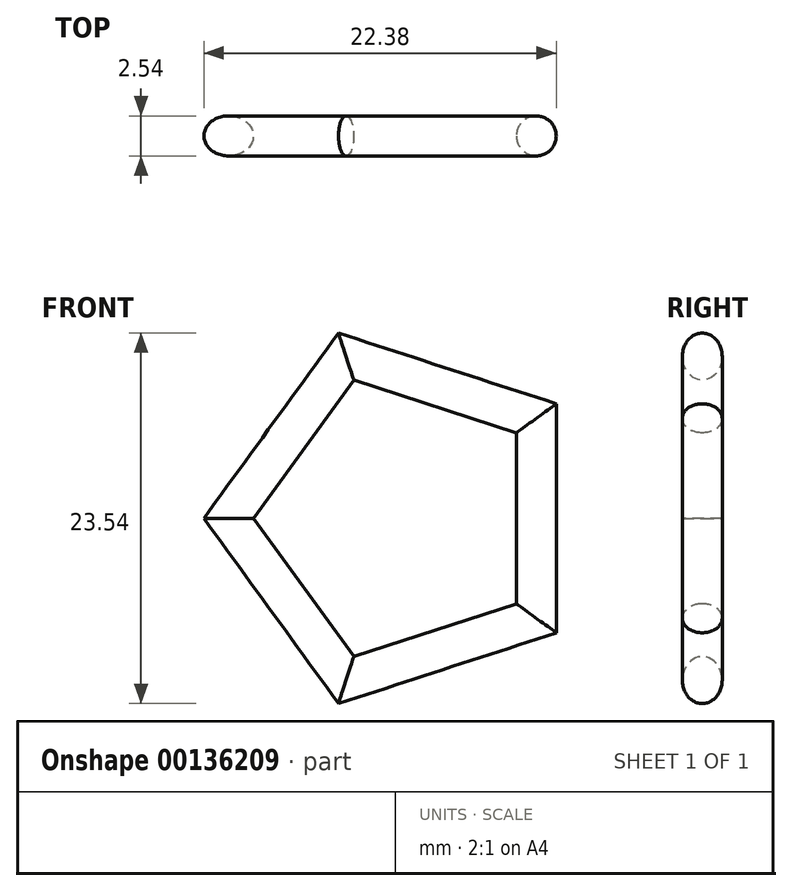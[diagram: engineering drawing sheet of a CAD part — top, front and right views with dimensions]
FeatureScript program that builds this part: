
annotation { "Feature Type Name" : "Feature", "Feature Type Description" : "" }
export const myFeature = defineFeature(function(context is Context, id is Id, definition is map)
    precondition{}
    {
        {
            var Q0;
            Q0=qCreatedBy(makeId("Front.planeOp"),FACE);
            var sketch = newSketch(context, id + "F0", { "sketchPlane" : qUnion([Q0])});
            skCircle(sketch, "E0.cCircle", {"center": v(0, 0) * mm, "radius": 11 * mm, "construction": true});
            skLineSegment(sketch, "E0.0", {"start": v(11, 6.35) * mm, "end": v(11, -6.35) * mm});
            skLineSegment(sketch, "E0.1", {"start": v(11, -6.35) * mm, "end": v(0, -12.7) * mm});
            skLineSegment(sketch, "E0.2", {"start": v(0, -12.7) * mm, "end": v(-11, -6.35) * mm});
            skLineSegment(sketch, "E0.3", {"start": v(-11, -6.35) * mm, "end": v(-11, 6.35) * mm});
            skLineSegment(sketch, "E0.4", {"start": v(-11, 6.35) * mm, "end": v(0, 12.7) * mm});
            skLineSegment(sketch, "E0.5", {"start": v(0, 12.7) * mm, "end": v(11, 6.35) * mm});
            skPoint(sketch, "E0.0.midPoint", {"position": v(11, 0) * mm});
            skSolve(sketch);
        }
        {
            var Q0;
            Q0=qCreatedBy(makeId("Front.planeOp"),FACE);
            var sketch = newSketch(context, id + "F1", { "sketchPlane" : qUnion([Q0])});
            skCircle(sketch, "E1.cCircle", {"center": v(2.26, 0) * mm, "radius": 8.74 * mm, "construction": true});
            skLineSegment(sketch, "E1.0", {"start": v(11, 6.35) * mm, "end": v(11, -6.35) * mm});
            skLineSegment(sketch, "E1.1", {"start": v(11, -6.35) * mm, "end": v(-1.08, -10.27) * mm});
            skLineSegment(sketch, "E1.2", {"start": v(-1.08, -10.27) * mm, "end": v(-8.54, 0) * mm});
            skLineSegment(sketch, "E1.3", {"start": v(-8.54, 0) * mm, "end": v(-1.08, 10.27) * mm});
            skLineSegment(sketch, "E1.4", {"start": v(-1.08, 10.27) * mm, "end": v(11, 6.35) * mm});
            skPoint(sketch, "E1.0.midPoint", {"position": v(11, 0) * mm});
            skSolve(sketch);
        }
        {
            var Q0;
            Q0=qCreatedBy(makeId("Top.planeOp"),FACE);
            var sketch = newSketch(context, id + "F2", { "sketchPlane" : qUnion([Q0])});
            skCircle(sketch, "E2", {"center": v(11, 0) * mm, "radius": 1.27 * mm});
            skSolve(sketch);
        }
        {
            var Q0;
            Q0=makeQuery(id+"F2.imprint","IMPRINT",FACE,{"disambiguationData":[TD([[makeQuery(id+"F2.imprint","IMPRINT",EDGE,{"derivedFrom":sQuery(id+"F2.wireOp",EDGE,"E2")}),1.0]])]});
            var Q1;
            Q1=sQuery(id+"F1.wireOp",EDGE,"E1.0");
            var Q2;
            Q2=sQuery(id+"F1.wireOp",EDGE,"E1.4");
            var Q3;
            Q3=sQuery(id+"F1.wireOp",EDGE,"E1.3");
            var Q4;
            Q4=sQuery(id+"F1.wireOp",EDGE,"E1.2");
            var Q5;
            Q5=sQuery(id+"F1.wireOp",EDGE,"E1.1");
            sweep(context, id + "F3", {"profiles" : qUnion([Q0]), "path" : qUnion([Q1, Q2, Q3, Q4, Q5])});
        }
    });
